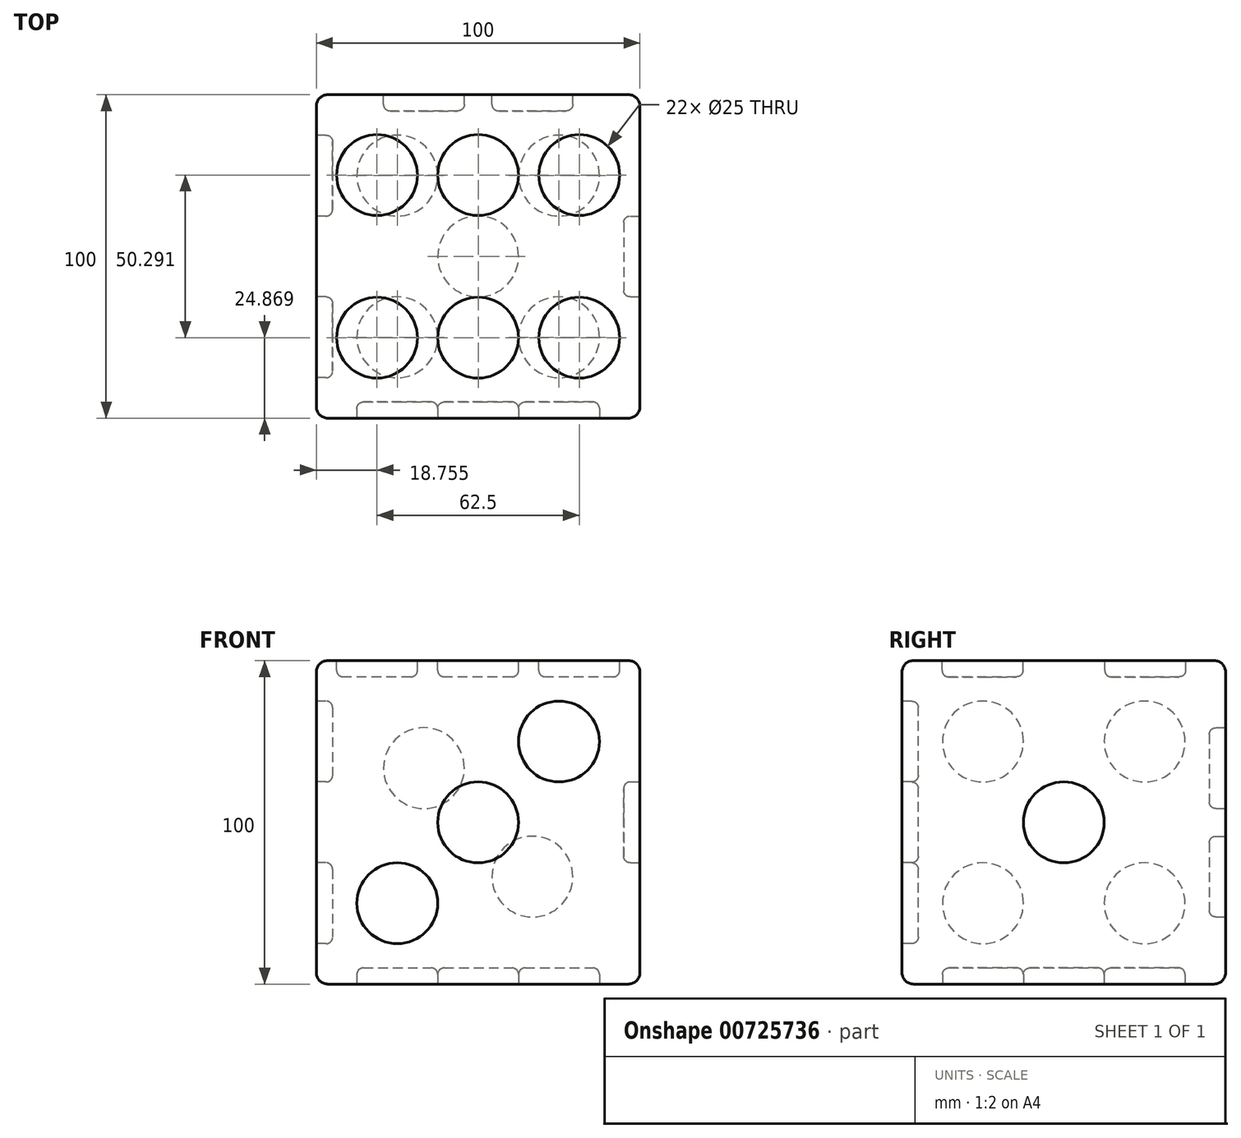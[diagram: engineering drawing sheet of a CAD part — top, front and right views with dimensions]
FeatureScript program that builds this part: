
annotation { "Feature Type Name" : "Feature", "Feature Type Description" : "" }
export const myFeature = defineFeature(function(context is Context, id is Id, definition is map)
    precondition{}
    {
        {
            var Q0;
            Q0=qCreatedBy(makeId("Top.planeOp"),FACE);
            var sketch = newSketch(context, id + "F0", { "sketchPlane" : qUnion([Q0])});
            skLineSegment(sketch, "E0.bottom", {"start": v(-56.38, -72.13) * mm, "end": v(-156.38, -72.13) * mm});
            skLineSegment(sketch, "E0.top", {"start": v(-56.38, 27.87) * mm, "end": v(-156.38, 27.87) * mm});
            skLineSegment(sketch, "E0.left", {"start": v(-56.38, -72.13) * mm, "end": v(-56.38, 27.87) * mm});
            skLineSegment(sketch, "E0.right", {"start": v(-156.38, -72.13) * mm, "end": v(-156.38, 27.87) * mm});
            skPoint(sketch, "E1.centerSnap0", {"position": v(-56.38, -22.13) * mm});
            skPoint(sketch, "E1.centerSnap1", {"position": v(-106.38, 27.87) * mm});
            skSolve(sketch);
        }
        {
            var Q0;
            Q0 = qSketchRegion(id + "F0", true);
            extrude(context, id + "F1", {"entities" : qUnion([Q0]), "depth" : 100 * mm, "offsetDistance" : 25 * mm});
        }
        {
            var Q0;
            Q0=makeQuery(id+"F1.opExtrude","SWEPT_FACE",FACE,{"disambiguationData":[OSD([sQuery(id+"F0.wireOp",EDGE,"E0.left")])]});
            var sketch = newSketch(context, id + "F2", { "sketchPlane" : qUnion([Q0])});
            skCircle(sketch, "E2", {"center": v(-22.13, 50) * mm, "radius": 12.5 * mm});
            skPoint(sketch, "E2.centerSnap0", {"position": v(-22.13, 100) * mm});
            skPoint(sketch, "E2.centerSnap1", {"position": v(27.87, 50) * mm});
            skSolve(sketch);
        }
        {
            var Q0;
            Q0=makeQuery(id+"F1.opExtrude","CAP_FACE",FACE,{"disambiguationData":[OSD([sQuery(id+"F0.wireOp",EDGE,"E0.bottom"),sQuery(id+"F0.wireOp",EDGE,"E0.top"),sQuery(id+"F0.wireOp",EDGE,"E0.left"),sQuery(id+"F0.wireOp",EDGE,"E0.right")])],"isStart":true});
            var sketch = newSketch(context, id + "F3", { "sketchPlane" : qUnion([Q0])});
            skCircle(sketch, "E3", {"center": v(-106.38, 22.13) * mm, "radius": 12.5 * mm});
            skCircle(sketch, "E4", {"center": v(-131.38, 47.13) * mm, "radius": 12.5 * mm});
            skCircle(sketch, "E5", {"center": v(-131.38, -2.87) * mm, "radius": 12.5 * mm});
            skCircle(sketch, "E6", {"center": v(-81.38, 47.13) * mm, "radius": 12.5 * mm});
            skCircle(sketch, "E7", {"center": v(-81.38, -2.87) * mm, "radius": 12.5 * mm});
            skPoint(sketch, "E8.orphan", {"position": v(-156.38, -27.87) * mm});
            skPoint(sketch, "E9.end.orphan", {"position": v(-56.38, -27.87) * mm});
            skPoint(sketch, "E10.end.orphan", {"position": v(-56.38, 72.13) * mm});
            skPoint(sketch, "E11.start.orphan", {"position": v(-156.38, 72.13) * mm});
            skSolve(sketch);
        }
        {
            var Q0;
            Q0=makeQuery(id+"F1.opExtrude","SWEPT_FACE",FACE,{"disambiguationData":[OSD([sQuery(id+"F0.wireOp",EDGE,"E0.top")])]});
            var sketch = newSketch(context, id + "F4", { "sketchPlane" : qUnion([Q0])});
            skCircle(sketch, "E12", {"center": v(89.6, 33.23) * mm, "radius": 12.5 * mm});
            skCircle(sketch, "E13", {"center": v(123.14, 66.77) * mm, "radius": 12.5 * mm});
            skPoint(sketch, "E14.orphan", {"position": v(56.38, 0) * mm});
            skPoint(sketch, "E15.end.orphan", {"position": v(156.38, 100) * mm});
            skSolve(sketch);
        }
        {
            var Q0;
            Q0=makeQuery(id+"F1.opExtrude","SWEPT_FACE",FACE,{"disambiguationData":[OSD([sQuery(id+"F0.wireOp",EDGE,"E0.bottom")])]});
            var sketch = newSketch(context, id + "F5", { "sketchPlane" : qUnion([Q0])});
            skCircle(sketch, "E16", {"center": v(-106.38, 50) * mm, "radius": 12.5 * mm});
            skCircle(sketch, "E17", {"center": v(-81.38, 75) * mm, "radius": 12.5 * mm});
            skCircle(sketch, "E18", {"center": v(-131.38, 25) * mm, "radius": 12.5 * mm});
            skPoint(sketch, "E19.orphan", {"position": v(-56.38, 100) * mm});
            skPoint(sketch, "E20.trimOffspring.end.orphan", {"position": v(-156.38, 0) * mm});
            skSolve(sketch);
        }
        {
            var Q0;
            Q0=makeQuery(id+"F1.opExtrude","SWEPT_FACE",FACE,{"disambiguationData":[OSD([sQuery(id+"F0.wireOp",EDGE,"E0.right")])]});
            var sketch = newSketch(context, id + "F6", { "sketchPlane" : qUnion([Q0])});
            skCircle(sketch, "E21", {"center": v(-2.87, 75) * mm, "radius": 12.5 * mm});
            skCircle(sketch, "E22", {"center": v(47.13, 75) * mm, "radius": 12.5 * mm});
            skCircle(sketch, "E23", {"center": v(47.13, 25) * mm, "radius": 12.5 * mm});
            skCircle(sketch, "E24", {"center": v(-2.87, 25) * mm, "radius": 12.5 * mm});
            skPoint(sketch, "E25.end.orphan", {"position": v(-2.87, 50) * mm});
            skPoint(sketch, "E25.start.orphan", {"position": v(-27.87, 50) * mm});
            skPoint(sketch, "E26.start.orphan", {"position": v(22.13, 50) * mm});
            skPoint(sketch, "E27.end.orphan", {"position": v(22.13, 75) * mm});
            skPoint(sketch, "E27.start.orphan", {"position": v(22.13, 100) * mm});
            skPoint(sketch, "E28.end.orphan", {"position": v(22.13, 0) * mm});
            skPoint(sketch, "E29.orphan", {"position": v(22.13, 25) * mm});
            skPoint(sketch, "E30.end.orphan", {"position": v(72.13, 50) * mm});
            skPoint(sketch, "E30.start.orphan", {"position": v(47.13, 50) * mm});
            skSolve(sketch);
        }
        {
            var Q0;
            Q0=makeQuery(id+"F1.opExtrude","CAP_FACE",FACE,{"disambiguationData":[OSD([sQuery(id+"F0.wireOp",EDGE,"E0.bottom"),sQuery(id+"F0.wireOp",EDGE,"E0.top"),sQuery(id+"F0.wireOp",EDGE,"E0.left"),sQuery(id+"F0.wireOp",EDGE,"E0.right")])],"isStart":false});
            var sketch = newSketch(context, id + "F7", { "sketchPlane" : qUnion([Q0])});
            skCircle(sketch, "E31", {"center": v(-106.38, -47.26) * mm, "radius": 12.5 * mm});
            skCircle(sketch, "E32", {"center": v(-106.38, 3.03) * mm, "radius": 12.5 * mm});
            skCircle(sketch, "E33", {"center": v(-137.63, -47.26) * mm, "radius": 12.5 * mm});
            skCircle(sketch, "E34", {"center": v(-137.63, 3.03) * mm, "radius": 12.5 * mm});
            skCircle(sketch, "E35", {"center": v(-75.13, 3.03) * mm, "radius": 12.5 * mm});
            skCircle(sketch, "E36", {"center": v(-75.13, -47.26) * mm, "radius": 12.5 * mm});
            skPoint(sketch, "E37.orphan", {"position": v(-106.38, -72.13) * mm});
            skPoint(sketch, "E38.trimOffspring.end.orphan", {"position": v(-56.38, -47.26) * mm});
            skPoint(sketch, "E39.orphan", {"position": v(-56.38, 3.03) * mm});
            skPoint(sketch, "E40.start.orphan", {"position": v(-156.38, -47.26) * mm});
            skPoint(sketch, "E41.trimOffspring.end.orphan", {"position": v(-118.88, -47.26) * mm});
            skPoint(sketch, "E42.start.orphan", {"position": v(-93.88, -47.26) * mm});
            skPoint(sketch, "E43.orphan", {"position": v(-156.38, 3.03) * mm});
            skPoint(sketch, "E44.end.orphan", {"position": v(-118.88, 3.03) * mm});
            skPoint(sketch, "E45.start.orphan", {"position": v(-93.88, 3.03) * mm});
            skPoint(sketch, "E46.orphan", {"position": v(-106.38, 27.87) * mm});
            skSolve(sketch);
        }
        {
            var Q0;
            Q0=makeQuery(id+"F3.imprint","IMPRINT",FACE,{"disambiguationData":[TD([[makeQuery(id+"F3.imprint","IMPRINT",EDGE,{"derivedFrom":sQuery(id+"F3.wireOp",EDGE,"E6")}),1.0]])]});
            var Q1;
            Q1=makeQuery(id+"F3.imprint","IMPRINT",FACE,{"disambiguationData":[TD([[makeQuery(id+"F3.imprint","IMPRINT",EDGE,{"derivedFrom":sQuery(id+"F3.wireOp",EDGE,"E3")}),1.0]])]});
            var Q2;
            Q2=makeQuery(id+"F3.imprint","IMPRINT",FACE,{"disambiguationData":[TD([[makeQuery(id+"F3.imprint","IMPRINT",EDGE,{"derivedFrom":sQuery(id+"F3.wireOp",EDGE,"E4")}),1.0]])]});
            var Q3;
            Q3=makeQuery(id+"F3.imprint","IMPRINT",FACE,{"disambiguationData":[TD([[makeQuery(id+"F3.imprint","IMPRINT",EDGE,{"derivedFrom":sQuery(id+"F3.wireOp",EDGE,"E5")}),1.0]])]});
            var Q4;
            Q4=makeQuery(id+"F3.imprint","IMPRINT",FACE,{"disambiguationData":[TD([[makeQuery(id+"F3.imprint","IMPRINT",EDGE,{"derivedFrom":sQuery(id+"F3.wireOp",EDGE,"E7")}),1.0]])]});
            extrude(context, id + "F8", {"entities" : qUnion([Q0, Q1, Q2, Q3, Q4]), "operationType" : NewBodyOperationType.REMOVE, "oppositeDirection" : true, "depth" : 5 * mm, "offsetDistance" : 25 * mm});
        }
        {
            var Q0;
            Q0=makeQuery(id+"F5.imprint","IMPRINT",FACE,{"disambiguationData":[TD([[makeQuery(id+"F5.imprint","IMPRINT",EDGE,{"derivedFrom":sQuery(id+"F5.wireOp",EDGE,"E17")}),1.0]])]});
            var Q1;
            Q1=makeQuery(id+"F5.imprint","IMPRINT",FACE,{"disambiguationData":[TD([[makeQuery(id+"F5.imprint","IMPRINT",EDGE,{"derivedFrom":sQuery(id+"F5.wireOp",EDGE,"E16")}),1.0]])]});
            var Q2;
            Q2=makeQuery(id+"F5.imprint","IMPRINT",FACE,{"disambiguationData":[TD([[makeQuery(id+"F5.imprint","IMPRINT",EDGE,{"derivedFrom":sQuery(id+"F5.wireOp",EDGE,"E18")}),1.0]])]});
            extrude(context, id + "F9", {"entities" : qUnion([Q0, Q1, Q2]), "operationType" : NewBodyOperationType.REMOVE, "oppositeDirection" : true, "depth" : 5 * mm, "offsetDistance" : 25 * mm});
        }
        {
            var Q0;
            Q0=makeQuery(id+"F2.imprint","IMPRINT",FACE,{"disambiguationData":[TD([[makeQuery(id+"F2.imprint","IMPRINT",EDGE,{"derivedFrom":sQuery(id+"F2.wireOp",EDGE,"E2")}),1.0]])]});
            extrude(context, id + "F10", {"entities" : qUnion([Q0]), "operationType" : NewBodyOperationType.REMOVE, "oppositeDirection" : true, "depth" : 5 * mm, "offsetDistance" : 25 * mm});
        }
        {
            var Q0;
            Q0=makeQuery(id+"F6.imprint","IMPRINT",FACE,{"disambiguationData":[TD([[makeQuery(id+"F6.imprint","IMPRINT",EDGE,{"derivedFrom":sQuery(id+"F6.wireOp",EDGE,"E21")}),1.0]])]});
            var Q1;
            Q1=makeQuery(id+"F6.imprint","IMPRINT",FACE,{"disambiguationData":[TD([[makeQuery(id+"F6.imprint","IMPRINT",EDGE,{"derivedFrom":sQuery(id+"F6.wireOp",EDGE,"E24")}),1.0]])]});
            var Q2;
            Q2=makeQuery(id+"F6.imprint","IMPRINT",FACE,{"disambiguationData":[TD([[makeQuery(id+"F6.imprint","IMPRINT",EDGE,{"derivedFrom":sQuery(id+"F6.wireOp",EDGE,"E23")}),1.0]])]});
            var Q3;
            Q3=makeQuery(id+"F6.imprint","IMPRINT",FACE,{"disambiguationData":[TD([[makeQuery(id+"F6.imprint","IMPRINT",EDGE,{"derivedFrom":sQuery(id+"F6.wireOp",EDGE,"E22")}),1.0]])]});
            extrude(context, id + "F11", {"entities" : qUnion([Q0, Q1, Q2, Q3]), "operationType" : NewBodyOperationType.REMOVE, "oppositeDirection" : true, "depth" : 5 * mm, "offsetDistance" : 25 * mm});
        }
        {
            var Q0;
            Q0=makeQuery(id+"F7.imprint","IMPRINT",FACE,{"disambiguationData":[TD([[makeQuery(id+"F7.imprint","IMPRINT",EDGE,{"derivedFrom":sQuery(id+"F7.wireOp",EDGE,"E35")}),1.0]])]});
            var Q1;
            Q1=makeQuery(id+"F7.imprint","IMPRINT",FACE,{"disambiguationData":[TD([[makeQuery(id+"F7.imprint","IMPRINT",EDGE,{"derivedFrom":sQuery(id+"F7.wireOp",EDGE,"E32")}),1.0]])]});
            var Q2;
            Q2=makeQuery(id+"F7.imprint","IMPRINT",FACE,{"disambiguationData":[TD([[makeQuery(id+"F7.imprint","IMPRINT",EDGE,{"derivedFrom":sQuery(id+"F7.wireOp",EDGE,"E36")}),1.0]])]});
            var Q3;
            Q3=makeQuery(id+"F7.imprint","IMPRINT",FACE,{"disambiguationData":[TD([[makeQuery(id+"F7.imprint","IMPRINT",EDGE,{"derivedFrom":sQuery(id+"F7.wireOp",EDGE,"E31")}),1.0]])]});
            var Q4;
            Q4=makeQuery(id+"F7.imprint","IMPRINT",FACE,{"disambiguationData":[TD([[makeQuery(id+"F7.imprint","IMPRINT",EDGE,{"derivedFrom":sQuery(id+"F7.wireOp",EDGE,"E33")}),1.0]])]});
            var Q5;
            Q5=makeQuery(id+"F7.imprint","IMPRINT",FACE,{"disambiguationData":[TD([[makeQuery(id+"F7.imprint","IMPRINT",EDGE,{"derivedFrom":sQuery(id+"F7.wireOp",EDGE,"E34")}),1.0]])]});
            extrude(context, id + "F12", {"entities" : qUnion([Q0, Q1, Q2, Q3, Q4, Q5]), "operationType" : NewBodyOperationType.REMOVE, "oppositeDirection" : true, "depth" : 5 * mm, "offsetDistance" : 25 * mm});
        }
        {
            var Q0;
            Q0=makeQuery(id+"F4.imprint","IMPRINT",FACE,{"disambiguationData":[TD([[makeQuery(id+"F4.imprint","IMPRINT",EDGE,{"derivedFrom":sQuery(id+"F4.wireOp",EDGE,"E12")}),1.0]])]});
            var Q1;
            Q1=makeQuery(id+"F4.imprint","IMPRINT",FACE,{"disambiguationData":[TD([[makeQuery(id+"F4.imprint","IMPRINT",EDGE,{"derivedFrom":sQuery(id+"F4.wireOp",EDGE,"E13")}),1.0]])]});
            extrude(context, id + "F13", {"entities" : qUnion([Q0, Q1]), "operationType" : NewBodyOperationType.REMOVE, "oppositeDirection" : true, "depth" : 5 * mm, "offsetDistance" : 25 * mm});
        }
        {
            var Q0;
            Q0=makeQuery(id+"F10.boolean.opBoolean","COPY",EDGE,{"derivedFrom":makeQuery(id+"F10.opExtrude","CAP_EDGE",EDGE,{"disambiguationData":[OSD([sQuery(id+"F2.wireOp",EDGE,"E2")])],"isStart":false})});
            var Q1;
            Q1=makeQuery(id+"F10.boolean.opBoolean","COPY",EDGE,{"derivedFrom":makeQuery(id+"F10.opExtrude","CAP_EDGE",EDGE,{"disambiguationData":[OSD([sQuery(id+"F2.wireOp",EDGE,"E2")])],"isStart":true})});
            fillet(context, id + "F14", {"entities" : qUnion([Q0, Q1]), "radius" : 2 * mm, "tangentPropagation" : true, "allowEdgeOverflow" : false});
        }
        {
            var Q0;
            Q0=makeQuery(id+"F9.boolean.opBoolean","COPY",EDGE,{"derivedFrom":makeQuery(id+"F9.opExtrude","CAP_EDGE",EDGE,{"disambiguationData":[OSD([sQuery(id+"F5.wireOp",EDGE,"E17")])],"isStart":false})});
            var Q1;
            Q1=makeQuery(id+"F9.boolean.opBoolean","COPY",EDGE,{"derivedFrom":makeQuery(id+"F9.opExtrude","CAP_EDGE",EDGE,{"disambiguationData":[OSD([sQuery(id+"F5.wireOp",EDGE,"E17")])],"isStart":true})});
            var Q2;
            Q2=makeQuery(id+"F9.boolean.opBoolean","COPY",EDGE,{"derivedFrom":makeQuery(id+"F9.opExtrude","CAP_EDGE",EDGE,{"disambiguationData":[OSD([sQuery(id+"F5.wireOp",EDGE,"E16")])],"isStart":false})});
            var Q3;
            Q3=makeQuery(id+"F9.boolean.opBoolean","COPY",EDGE,{"derivedFrom":makeQuery(id+"F9.opExtrude","CAP_EDGE",EDGE,{"disambiguationData":[OSD([sQuery(id+"F5.wireOp",EDGE,"E16")])],"isStart":true})});
            var Q4;
            Q4=makeQuery(id+"F9.boolean.opBoolean","COPY",EDGE,{"derivedFrom":makeQuery(id+"F9.opExtrude","CAP_EDGE",EDGE,{"disambiguationData":[OSD([sQuery(id+"F5.wireOp",EDGE,"E18")])],"isStart":false})});
            var Q5;
            Q5=makeQuery(id+"F9.boolean.opBoolean","COPY",EDGE,{"derivedFrom":makeQuery(id+"F9.opExtrude","CAP_EDGE",EDGE,{"disambiguationData":[OSD([sQuery(id+"F5.wireOp",EDGE,"E18")])],"isStart":true})});
            fillet(context, id + "F15", {"entities" : qUnion([Q0, Q1, Q2, Q3, Q4, Q5]), "radius" : 2 * mm, "tangentPropagation" : true, "allowEdgeOverflow" : false});
        }
        {
            var Q0;
            Q0=makeQuery(id+"F11.boolean.opBoolean","COPY",EDGE,{"derivedFrom":makeQuery(id+"F11.opExtrude","CAP_EDGE",EDGE,{"disambiguationData":[OSD([sQuery(id+"F6.wireOp",EDGE,"E21")])],"isStart":false})});
            var Q1;
            Q1=makeQuery(id+"F11.boolean.opBoolean","COPY",EDGE,{"derivedFrom":makeQuery(id+"F11.opExtrude","CAP_EDGE",EDGE,{"disambiguationData":[OSD([sQuery(id+"F6.wireOp",EDGE,"E21")])],"isStart":true})});
            var Q2;
            Q2=makeQuery(id+"F11.boolean.opBoolean","COPY",EDGE,{"derivedFrom":makeQuery(id+"F11.opExtrude","CAP_EDGE",EDGE,{"disambiguationData":[OSD([sQuery(id+"F6.wireOp",EDGE,"E22")])],"isStart":false})});
            var Q3;
            Q3=makeQuery(id+"F11.boolean.opBoolean","COPY",EDGE,{"derivedFrom":makeQuery(id+"F11.opExtrude","CAP_EDGE",EDGE,{"disambiguationData":[OSD([sQuery(id+"F6.wireOp",EDGE,"E22")])],"isStart":true})});
            var Q4;
            Q4=makeQuery(id+"F11.boolean.opBoolean","COPY",EDGE,{"derivedFrom":makeQuery(id+"F11.opExtrude","CAP_EDGE",EDGE,{"disambiguationData":[OSD([sQuery(id+"F6.wireOp",EDGE,"E23")])],"isStart":false})});
            var Q5;
            Q5=makeQuery(id+"F11.boolean.opBoolean","COPY",EDGE,{"derivedFrom":makeQuery(id+"F11.opExtrude","CAP_EDGE",EDGE,{"disambiguationData":[OSD([sQuery(id+"F6.wireOp",EDGE,"E23")])],"isStart":true})});
            var Q6;
            Q6=makeQuery(id+"F11.boolean.opBoolean","COPY",EDGE,{"derivedFrom":makeQuery(id+"F11.opExtrude","CAP_EDGE",EDGE,{"disambiguationData":[OSD([sQuery(id+"F6.wireOp",EDGE,"E24")])],"isStart":false})});
            var Q7;
            Q7=makeQuery(id+"F11.boolean.opBoolean","COPY",EDGE,{"derivedFrom":makeQuery(id+"F11.opExtrude","CAP_EDGE",EDGE,{"disambiguationData":[OSD([sQuery(id+"F6.wireOp",EDGE,"E24")])],"isStart":true})});
            fillet(context, id + "F16", {"entities" : qUnion([Q0, Q1, Q2, Q3, Q4, Q5, Q6, Q7]), "radius" : 2 * mm, "tangentPropagation" : true, "allowEdgeOverflow" : false});
        }
        {
            var Q0;
            Q0=makeQuery(id+"F13.boolean.opBoolean","COPY",EDGE,{"derivedFrom":makeQuery(id+"F13.opExtrude","CAP_EDGE",EDGE,{"disambiguationData":[OSD([sQuery(id+"F4.wireOp",EDGE,"E12")])],"isStart":false})});
            var Q1;
            Q1=makeQuery(id+"F13.boolean.opBoolean","COPY",EDGE,{"derivedFrom":makeQuery(id+"F13.opExtrude","CAP_EDGE",EDGE,{"disambiguationData":[OSD([sQuery(id+"F4.wireOp",EDGE,"E12")])],"isStart":true})});
            var Q2;
            Q2=makeQuery(id+"F13.boolean.opBoolean","COPY",EDGE,{"derivedFrom":makeQuery(id+"F13.opExtrude","CAP_EDGE",EDGE,{"disambiguationData":[OSD([sQuery(id+"F4.wireOp",EDGE,"E13")])],"isStart":false})});
            var Q3;
            Q3=makeQuery(id+"F13.boolean.opBoolean","COPY",EDGE,{"derivedFrom":makeQuery(id+"F13.opExtrude","CAP_EDGE",EDGE,{"disambiguationData":[OSD([sQuery(id+"F4.wireOp",EDGE,"E13")])],"isStart":true})});
            fillet(context, id + "F17", {"entities" : qUnion([Q0, Q1, Q2, Q3]), "radius" : 2 * mm, "tangentPropagation" : true, "allowEdgeOverflow" : false});
        }
        {
            var Q0;
            Q0=makeQuery(id+"F12.boolean.opBoolean","COPY",EDGE,{"derivedFrom":makeQuery(id+"F12.opExtrude","CAP_EDGE",EDGE,{"disambiguationData":[OSD([sQuery(id+"F7.wireOp",EDGE,"E35")])],"isStart":false})});
            var Q1;
            Q1=makeQuery(id+"F12.boolean.opBoolean","COPY",EDGE,{"derivedFrom":makeQuery(id+"F12.opExtrude","CAP_EDGE",EDGE,{"disambiguationData":[OSD([sQuery(id+"F7.wireOp",EDGE,"E35")])],"isStart":true})});
            var Q2;
            Q2=makeQuery(id+"F12.boolean.opBoolean","COPY",EDGE,{"derivedFrom":makeQuery(id+"F12.opExtrude","CAP_EDGE",EDGE,{"disambiguationData":[OSD([sQuery(id+"F7.wireOp",EDGE,"E32")])],"isStart":false})});
            var Q3;
            Q3=makeQuery(id+"F12.boolean.opBoolean","COPY",EDGE,{"derivedFrom":makeQuery(id+"F12.opExtrude","CAP_EDGE",EDGE,{"disambiguationData":[OSD([sQuery(id+"F7.wireOp",EDGE,"E32")])],"isStart":true})});
            var Q4;
            Q4=makeQuery(id+"F12.boolean.opBoolean","COPY",EDGE,{"derivedFrom":makeQuery(id+"F12.opExtrude","CAP_EDGE",EDGE,{"disambiguationData":[OSD([sQuery(id+"F7.wireOp",EDGE,"E34")])],"isStart":false})});
            var Q5;
            Q5=makeQuery(id+"F12.boolean.opBoolean","COPY",EDGE,{"derivedFrom":makeQuery(id+"F12.opExtrude","CAP_EDGE",EDGE,{"disambiguationData":[OSD([sQuery(id+"F7.wireOp",EDGE,"E34")])],"isStart":true})});
            var Q6;
            Q6=makeQuery(id+"F12.boolean.opBoolean","COPY",EDGE,{"derivedFrom":makeQuery(id+"F12.opExtrude","CAP_EDGE",EDGE,{"disambiguationData":[OSD([sQuery(id+"F7.wireOp",EDGE,"E36")])],"isStart":false})});
            var Q7;
            Q7=makeQuery(id+"F12.boolean.opBoolean","COPY",EDGE,{"derivedFrom":makeQuery(id+"F12.opExtrude","CAP_EDGE",EDGE,{"disambiguationData":[OSD([sQuery(id+"F7.wireOp",EDGE,"E36")])],"isStart":true})});
            var Q8;
            Q8=makeQuery(id+"F12.boolean.opBoolean","COPY",EDGE,{"derivedFrom":makeQuery(id+"F12.opExtrude","CAP_EDGE",EDGE,{"disambiguationData":[OSD([sQuery(id+"F7.wireOp",EDGE,"E31")])],"isStart":false})});
            var Q9;
            Q9=makeQuery(id+"F12.boolean.opBoolean","COPY",EDGE,{"derivedFrom":makeQuery(id+"F12.opExtrude","CAP_EDGE",EDGE,{"disambiguationData":[OSD([sQuery(id+"F7.wireOp",EDGE,"E31")])],"isStart":true})});
            var Q10;
            Q10=makeQuery(id+"F12.boolean.opBoolean","COPY",EDGE,{"derivedFrom":makeQuery(id+"F12.opExtrude","CAP_EDGE",EDGE,{"disambiguationData":[OSD([sQuery(id+"F7.wireOp",EDGE,"E33")])],"isStart":false})});
            var Q11;
            Q11=makeQuery(id+"F12.boolean.opBoolean","COPY",EDGE,{"derivedFrom":makeQuery(id+"F12.opExtrude","CAP_EDGE",EDGE,{"disambiguationData":[OSD([sQuery(id+"F7.wireOp",EDGE,"E33")])],"isStart":true})});
            fillet(context, id + "F18", {"entities" : qUnion([Q0, Q1, Q2, Q3, Q4, Q5, Q6, Q7, Q8, Q9, Q10, Q11]), "radius" : 2 * mm, "tangentPropagation" : true, "allowEdgeOverflow" : false});
        }
        {
            var Q0;
            Q0=makeQuery(id+"F8.boolean.opBoolean","COPY",EDGE,{"derivedFrom":makeQuery(id+"F8.opExtrude","CAP_EDGE",EDGE,{"disambiguationData":[OSD([sQuery(id+"F3.wireOp",EDGE,"E5")])],"isStart":false})});
            var Q1;
            Q1=makeQuery(id+"F8.boolean.opBoolean","COPY",EDGE,{"derivedFrom":makeQuery(id+"F8.opExtrude","CAP_EDGE",EDGE,{"disambiguationData":[OSD([sQuery(id+"F3.wireOp",EDGE,"E5")])],"isStart":true})});
            var Q2;
            Q2=makeQuery(id+"F8.boolean.opBoolean","COPY",EDGE,{"derivedFrom":makeQuery(id+"F8.opExtrude","CAP_EDGE",EDGE,{"disambiguationData":[OSD([sQuery(id+"F3.wireOp",EDGE,"E3")])],"isStart":false})});
            var Q3;
            Q3=makeQuery(id+"F8.boolean.opBoolean","COPY",EDGE,{"derivedFrom":makeQuery(id+"F8.opExtrude","CAP_EDGE",EDGE,{"disambiguationData":[OSD([sQuery(id+"F3.wireOp",EDGE,"E3")])],"isStart":true})});
            var Q4;
            Q4=makeQuery(id+"F8.boolean.opBoolean","COPY",EDGE,{"derivedFrom":makeQuery(id+"F8.opExtrude","CAP_EDGE",EDGE,{"disambiguationData":[OSD([sQuery(id+"F3.wireOp",EDGE,"E7")])],"isStart":false})});
            var Q5;
            Q5=makeQuery(id+"F8.boolean.opBoolean","COPY",EDGE,{"derivedFrom":makeQuery(id+"F8.opExtrude","CAP_EDGE",EDGE,{"disambiguationData":[OSD([sQuery(id+"F3.wireOp",EDGE,"E7")])],"isStart":true})});
            var Q6;
            Q6=makeQuery(id+"F8.boolean.opBoolean","COPY",EDGE,{"derivedFrom":makeQuery(id+"F8.opExtrude","CAP_EDGE",EDGE,{"disambiguationData":[OSD([sQuery(id+"F3.wireOp",EDGE,"E4")])],"isStart":false})});
            var Q7;
            Q7=makeQuery(id+"F8.boolean.opBoolean","COPY",EDGE,{"derivedFrom":makeQuery(id+"F8.opExtrude","CAP_EDGE",EDGE,{"disambiguationData":[OSD([sQuery(id+"F3.wireOp",EDGE,"E4")])],"isStart":true})});
            var Q8;
            Q8=makeQuery(id+"F8.boolean.opBoolean","COPY",EDGE,{"derivedFrom":makeQuery(id+"F8.opExtrude","CAP_EDGE",EDGE,{"disambiguationData":[OSD([sQuery(id+"F3.wireOp",EDGE,"E6")])],"isStart":false})});
            var Q9;
            Q9=makeQuery(id+"F8.boolean.opBoolean","COPY",EDGE,{"derivedFrom":makeQuery(id+"F8.opExtrude","CAP_EDGE",EDGE,{"disambiguationData":[OSD([sQuery(id+"F3.wireOp",EDGE,"E6")])],"isStart":true})});
            fillet(context, id + "F19", {"entities" : qUnion([Q0, Q1, Q2, Q3, Q4, Q5, Q6, Q7, Q8, Q9]), "radius" : 2 * mm, "tangentPropagation" : true, "allowEdgeOverflow" : false});
        }
        {
            var Q0;
            Q0=makeQuery(id+"F1.opExtrude","CAP_EDGE",EDGE,{"disambiguationData":[OSD([sQuery(id+"F0.wireOp",EDGE,"E0.top")])],"isStart":false});
            var Q1;
            Q1=makeQuery(id+"F1.opExtrude","CAP_EDGE",EDGE,{"disambiguationData":[OSD([sQuery(id+"F0.wireOp",EDGE,"E0.right")])],"isStart":false});
            var Q2;
            Q2=makeQuery(id+"F1.opExtrude","SWEPT_EDGE",EDGE,{"disambiguationData":[OSD([sQuery(id+"F0.wireOp",EDGE,"E0.top"),sQuery(id+"F0.wireOp",EDGE,"E0.right")])]});
            var Q3;
            Q3=makeQuery(id+"F1.opExtrude","CAP_EDGE",EDGE,{"disambiguationData":[OSD([sQuery(id+"F0.wireOp",EDGE,"E0.bottom")])],"isStart":false});
            var Q4;
            Q4=makeQuery(id+"F1.opExtrude","SWEPT_EDGE",EDGE,{"disambiguationData":[OSD([sQuery(id+"F0.wireOp",EDGE,"E0.bottom"),sQuery(id+"F0.wireOp",EDGE,"E0.left")])]});
            var Q5;
            Q5=makeQuery(id+"F1.opExtrude","CAP_EDGE",EDGE,{"disambiguationData":[OSD([sQuery(id+"F0.wireOp",EDGE,"E0.left")])],"isStart":false});
            var Q6;
            Q6=makeQuery(id+"F1.opExtrude","CAP_EDGE",EDGE,{"disambiguationData":[OSD([sQuery(id+"F0.wireOp",EDGE,"E0.left")])],"isStart":true});
            var Q7;
            Q7=makeQuery(id+"F1.opExtrude","CAP_EDGE",EDGE,{"disambiguationData":[OSD([sQuery(id+"F0.wireOp",EDGE,"E0.bottom")])],"isStart":true});
            var Q8;
            Q8=makeQuery(id+"F1.opExtrude","CAP_EDGE",EDGE,{"disambiguationData":[OSD([sQuery(id+"F0.wireOp",EDGE,"E0.right")])],"isStart":true});
            var Q9;
            Q9=makeQuery(id+"F1.opExtrude","CAP_EDGE",EDGE,{"disambiguationData":[OSD([sQuery(id+"F0.wireOp",EDGE,"E0.top")])],"isStart":true});
            var Q10;
            Q10=makeQuery(id+"F1.opExtrude","SWEPT_EDGE",EDGE,{"disambiguationData":[OSD([sQuery(id+"F0.wireOp",EDGE,"E0.top"),sQuery(id+"F0.wireOp",EDGE,"E0.left")])]});
            var Q11;
            Q11=makeQuery(id+"F1.opExtrude","SWEPT_EDGE",EDGE,{"disambiguationData":[OSD([sQuery(id+"F0.wireOp",EDGE,"E0.bottom"),sQuery(id+"F0.wireOp",EDGE,"E0.right")])]});
            fillet(context, id + "F20", {"entities" : qUnion([Q0, Q1, Q2, Q3, Q4, Q5, Q6, Q7, Q8, Q9, Q10, Q11]), "radius" : 3.5 * mm, "tangentPropagation" : true, "allowEdgeOverflow" : false});
        }
    });
